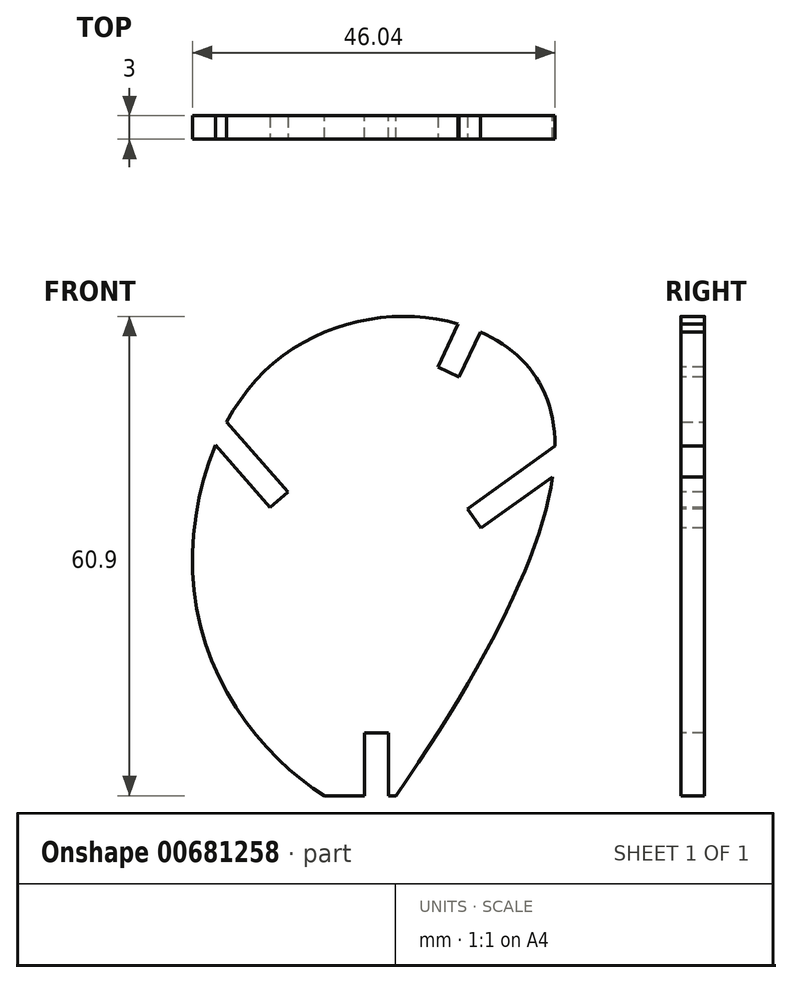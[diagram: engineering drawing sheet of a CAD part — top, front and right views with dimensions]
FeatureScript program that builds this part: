
annotation { "Feature Type Name" : "Feature", "Feature Type Description" : "" }
export const myFeature = defineFeature(function(context is Context, id is Id, definition is map)
    precondition{}
    {
        {
            assignVariable(context, id + "F0", {"name" : "MaterialDepth", "anyValue" : 3 * mm});
        }
        {
            var Q0;
            Q0=qCreatedBy(makeId("Front.planeOp"),FACE);
            var sketch = newSketch(context, id + "F1", { "sketchPlane" : qUnion([Q0])});
            skLineSegment(sketch, "E0", {"start": v(0, 53.6) * mm, "end": v(0, -7.3) * mm, "construction": true});
            skFitSpline(sketch, "E1", {"points": [v(-6.58, 0) * mm, v(-22.5, 22) * mm, v(-15.2, 52.94) * mm, v(6.9, 60.67) * mm, v(21.7, 50.29) * mm, v(2.48, 0) * mm], "startDerivative": vector(-102.35, 61.83) * mm, "endDerivative": vector(-172.56, -250.25) * mm});
            skLineSegment(sketch, "E2", {"start": v(-6.58, 0) * mm, "end": v(2.48, 0) * mm});
            skSolve(sketch);
        }
        {
            var Q0;
            Q0=makeQuery(id+"F1.imprint","IMPRINT",FACE,{"disambiguationData":[TD([[makeQuery(id+"F1.imprint","IMPRINT",EDGE,{"derivedFrom":sQuery(id+"F1.wireOp",EDGE,"E1")}),-1.0]])]});
            extrude(context, id + "F2", {"entities" : qUnion([Q0]), "endBound" : BoundingType.SYMMETRIC, "depth" : getVariable(context, 'MaterialDepth'), "offsetDistance" : 25 * mm});
        }
        {
            var Q0;
            Q0=makeQuery(id+"F2.opExtrude","CAP_FACE",FACE,{"disambiguationData":[OSD([sQuery(id+"F1.wireOp",EDGE,"E1"),sQuery(id+"F1.wireOp",EDGE,"E2")])],"isStart":false});
            var sketch = newSketch(context, id + "F3", { "sketchPlane" : qUnion([Q0])});
            skPoint(sketch, "E3", {"position": v(-19.78, 46.06) * mm});
            skLineSegment(sketch, "E4", {"start": v(-19.78, 46.06) * mm, "end": v(-16.4, 42.2) * mm, "construction": true});
            skLineSegment(sketch, "E5", {"start": v(-22.55, 43.63) * mm, "end": v(-19.78, 46.06) * mm, "construction": true});
            skLineSegment(sketch, "E6", {"start": v(-28.3, 53.53) * mm, "end": v(-27.18, 54.52) * mm});
            skLineSegment(sketch, "E7.MirrorCS", {"start": v(-13.5, 36.6) * mm, "end": v(-12.37, 37.6) * mm});
            skLineSegment(sketch, "E8", {"start": v(-28.3, 53.53) * mm, "end": v(-13.5, 36.6) * mm});
            skLineSegment(sketch, "E9.MirrorCS", {"start": v(-26.05, 55.5) * mm, "end": v(-27.18, 54.52) * mm});
            skLineSegment(sketch, "E10.MirrorCS", {"start": v(-26.05, 55.5) * mm, "end": v(-11.24, 38.58) * mm});
            skLineSegment(sketch, "E11.MirrorCS", {"start": v(-11.24, 38.58) * mm, "end": v(-12.37, 37.6) * mm});
            skPoint(sketch, "E12", {"position": v(11.79, 59.5) * mm});
            skLineSegment(sketch, "E13", {"start": v(11.79, 59.5) * mm, "end": v(7.5, 50.32) * mm, "construction": true});
            skLineSegment(sketch, "E14", {"start": v(11.79, 59.5) * mm, "end": v(20.67, 55.34) * mm, "construction": true});
            skLineSegment(sketch, "E15", {"start": v(10.5, 53.2) * mm, "end": v(9.14, 53.83) * mm});
            skLineSegment(sketch, "E16.MirrorCS", {"start": v(15.8, 64.52) * mm, "end": v(14.43, 65.16) * mm});
            skLineSegment(sketch, "E17", {"start": v(10.5, 53.2) * mm, "end": v(15.8, 64.52) * mm});
            skLineSegment(sketch, "E18.MirrorCS", {"start": v(7.78, 54.47) * mm, "end": v(9.14, 53.83) * mm});
            skLineSegment(sketch, "E19.MirrorCS", {"start": v(7.78, 54.47) * mm, "end": v(13.08, 65.8) * mm});
            skLineSegment(sketch, "E20.MirrorCS", {"start": v(13.08, 65.8) * mm, "end": v(14.43, 65.16) * mm});
            skPoint(sketch, "E21", {"position": v(22.58, 42.51) * mm});
            skLineSegment(sketch, "E22", {"start": v(36.33, 52.36) * mm, "end": v(22.58, 42.51) * mm, "construction": true});
            skLineSegment(sketch, "E23", {"start": v(22.58, 42.51) * mm, "end": v(29.15, 33.34) * mm, "construction": true});
            skLineSegment(sketch, "E24", {"start": v(33.62, 48.57) * mm, "end": v(32.74, 49.8) * mm});
            skLineSegment(sketch, "E25.MirrorCS", {"start": v(13.3, 34.01) * mm, "end": v(12.42, 35.23) * mm});
            skLineSegment(sketch, "E26", {"start": v(13.3, 34.01) * mm, "end": v(33.62, 48.57) * mm});
            skLineSegment(sketch, "E27.MirrorCS", {"start": v(11.55, 36.45) * mm, "end": v(31.87, 51.01) * mm});
            skLineSegment(sketch, "E28.MirrorCS", {"start": v(31.87, 51.01) * mm, "end": v(32.74, 49.8) * mm});
            skLineSegment(sketch, "E29.MirrorCS", {"start": v(11.55, 36.45) * mm, "end": v(12.42, 35.23) * mm});
            skLineSegment(sketch, "E30.bottom", {"start": v(1.5, -8) * mm, "end": v(-1.5, -8) * mm});
            skLineSegment(sketch, "E30.top", {"start": v(1.5, 8) * mm, "end": v(-1.5, 8) * mm});
            skLineSegment(sketch, "E30.left", {"start": v(1.5, -8) * mm, "end": v(1.5, 8) * mm});
            skLineSegment(sketch, "E30.right", {"start": v(-1.5, -8) * mm, "end": v(-1.5, 8) * mm});
            skPoint(sketch, "E30.middle", {"position": v(0, 0) * mm});
            skSolve(sketch);
        }
        {
            var Q0;
            Q0 = qSketchRegion(id + "F3", true);
            extrude(context, id + "F4", {"entities" : qUnion([Q0]), "operationType" : NewBodyOperationType.REMOVE, "oppositeDirection" : true, "depth" : 25 * mm, "offsetDistance" : 25 * mm});
        }
    });
